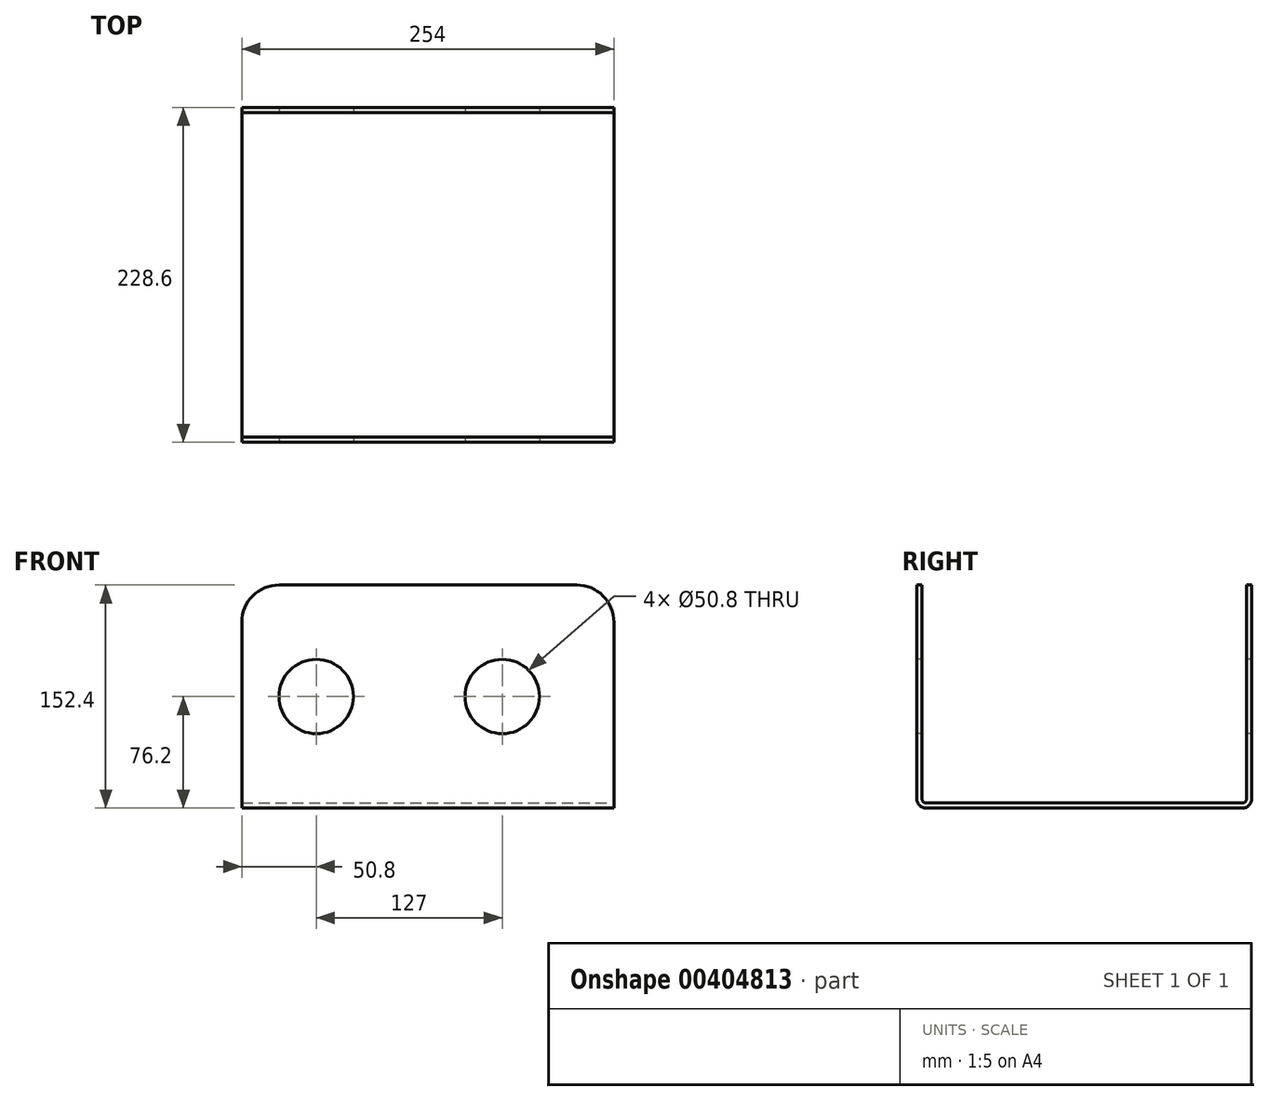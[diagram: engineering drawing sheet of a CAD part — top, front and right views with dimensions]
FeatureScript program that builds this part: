
annotation { "Feature Type Name" : "Feature", "Feature Type Description" : "" }
export const myFeature = defineFeature(function(context is Context, id is Id, definition is map)
    precondition{}
    {
        {
            var Q0;
            Q0=qCreatedBy(makeId("Front.planeOp"),FACE);
            var sketch = newSketch(context, id + "F0", { "sketchPlane" : qUnion([Q0])});
            skLineSegment(sketch, "E0.bottom", {"start": v(-101.6, 152.4) * mm, "end": v(101.6, 152.4) * mm});
            skLineSegment(sketch, "E0.top", {"start": v(-127, 0) * mm, "end": v(127, 0) * mm});
            skLineSegment(sketch, "E0.left", {"start": v(-127, 127) * mm, "end": v(-127, 0) * mm});
            skLineSegment(sketch, "E0.right", {"start": v(127, 127) * mm, "end": v(127, 0) * mm});
            skPoint(sketch, "E1.visualSharp", {"position": v(-127, 152.4) * mm});
            skArc(sketch, "E1.filletArc", {"start": v(-101.6, 152.4) * mm, "mid": v(-119.56, 144.96) * mm, "end": v(-127, 127) * mm});
            skPoint(sketch, "E2.visualSharp", {"position": v(127, 152.4) * mm});
            skArc(sketch, "E2.filletArc", {"start": v(127, 127) * mm, "mid": v(119.56, 144.96) * mm, "end": v(101.6, 152.4) * mm});
            skSolve(sketch);
        }
        {
            var Q0;
            Q0=makeQuery(id+"F0.imprint","IMPRINT",FACE,{"disambiguationData":[TD([[makeQuery(id+"F0.imprint","IMPRINT",EDGE,{"derivedFrom":sQuery(id+"F0.wireOp",EDGE,"E0.bottom")}),-1.0]])]});
            extrude(context, id + "F1", {"entities" : qUnion([Q0]), "depth" : 228.6 * mm});
        }
        {
            var Q0;
            Q0=makeQuery(id+"F1.opExtrude","CAP_FACE",FACE,{"disambiguationData":[OSD([sQuery(id+"F0.wireOp",EDGE,"E0.bottom"),sQuery(id+"F0.wireOp",EDGE,"E0.top"),sQuery(id+"F0.wireOp",EDGE,"E0.left"),sQuery(id+"F0.wireOp",EDGE,"E0.right"),sQuery(id+"F0.wireOp",EDGE,"E1.filletArc"),sQuery(id+"F0.wireOp",EDGE,"E2.filletArc")])],"isStart":false});
            var sketch = newSketch(context, id + "F2", { "sketchPlane" : qUnion([Q0])});
            skCircle(sketch, "E3", {"center": v(-76.2, 76.2) * mm, "radius": 25.4 * mm});
            skCircle(sketch, "E4", {"center": v(50.8, 76.2) * mm, "radius": 25.4 * mm});
            skLineSegment(sketch, "E5", {"start": v(-76.2, 76.2) * mm, "end": v(50.8, 76.2) * mm, "construction": true});
            skSolve(sketch);
        }
        {
            var Q0;
            Q0 = qSketchRegion(id + "F2", true);
            extrude(context, id + "F3", {"entities" : qUnion([Q0]), "operationType" : NewBodyOperationType.REMOVE, "endBound" : BoundingType.THROUGH_ALL, "oppositeDirection" : true, "depth" : 25.4 * mm});
        }
        {
            var Q0;
            Q0=makeQuery(id+"F1.opExtrude","SWEPT_FACE",FACE,{"disambiguationData":[OSD([sQuery(id+"F0.wireOp",EDGE,"E0.right")])]});
            var Q1;
            Q1=makeQuery(id+"F1.opExtrude","SWEPT_FACE",FACE,{"disambiguationData":[OSD([sQuery(id+"F0.wireOp",EDGE,"E2.filletArc")])]});
            var Q2;
            Q2=makeQuery(id+"F1.opExtrude","SWEPT_FACE",FACE,{"disambiguationData":[OSD([sQuery(id+"F0.wireOp",EDGE,"E0.bottom")])]});
            var Q3;
            Q3=makeQuery(id+"F1.opExtrude","SWEPT_FACE",FACE,{"disambiguationData":[OSD([sQuery(id+"F0.wireOp",EDGE,"E0.left")])]});
            var Q4;
            Q4=makeQuery(id+"F1.opExtrude","SWEPT_FACE",FACE,{"disambiguationData":[OSD([sQuery(id+"F0.wireOp",EDGE,"E1.filletArc")])]});
            var Q5;
            Q5=makeQuery(id+"F3.boolean.opBoolean","COPY",FACE,{"derivedFrom":makeQuery(id+"F3.opExtrude","SWEPT_FACE",FACE,{"disambiguationData":[OSD([sQuery(id+"F2.wireOp",EDGE,"E3")])]})});
            var Q6;
            Q6=makeQuery(id+"F3.boolean.opBoolean","COPY",FACE,{"derivedFrom":makeQuery(id+"F3.opExtrude","SWEPT_FACE",FACE,{"disambiguationData":[OSD([sQuery(id+"F2.wireOp",EDGE,"E4")])]})});
            shell(context, id + "F4", {"entities" : qUnion([Q0, Q1, Q2, Q3, Q4, Q5, Q6]), "thickness" : 3.42 * mm});
        }
        {
            var Q0;
            Q0=makeQuery(id+"F1.opExtrude","CAP_EDGE",EDGE,{"disambiguationData":[OSD([sQuery(id+"F0.wireOp",EDGE,"E0.top")])],"isStart":true});
            var Q1;
            Q1=makeQuery(id+"F1.opExtrude","CAP_EDGE",EDGE,{"disambiguationData":[OSD([sQuery(id+"F0.wireOp",EDGE,"E0.top")])],"isStart":false});
            fillet(context, id + "F5", {"entities" : qUnion([Q0, Q1]), "radius" : 6.35 * mm, "tangentPropagation" : true, "allowEdgeOverflow" : false});
        }
        {
            var Q0;
            {var subQ0=sQuery(id+"F0.wireOp",EDGE,"E0.top");Q0=makeQuery(id+"F4.opShell","OFFSET_EDGE",EDGE,{"disambiguationData":[OSD([subQ0]),TDD([makeQuery(id+"F1.opExtrude","CAP_EDGE",EDGE,{"disambiguationData":[OSD([subQ0])],"isStart":true})])]});}
            var Q1;
            {var subQ0=sQuery(id+"F0.wireOp",EDGE,"E0.top");Q1=makeQuery(id+"F4.opShell","OFFSET_EDGE",EDGE,{"disambiguationData":[OSD([subQ0]),TDD([makeQuery(id+"F1.opExtrude","CAP_EDGE",EDGE,{"disambiguationData":[OSD([subQ0])],"isStart":false})])]});}
            fillet(context, id + "F6", {"entities" : qUnion([Q0, Q1]), "radius" : 3.17 * mm, "tangentPropagation" : true, "allowEdgeOverflow" : false});
        }
    });
